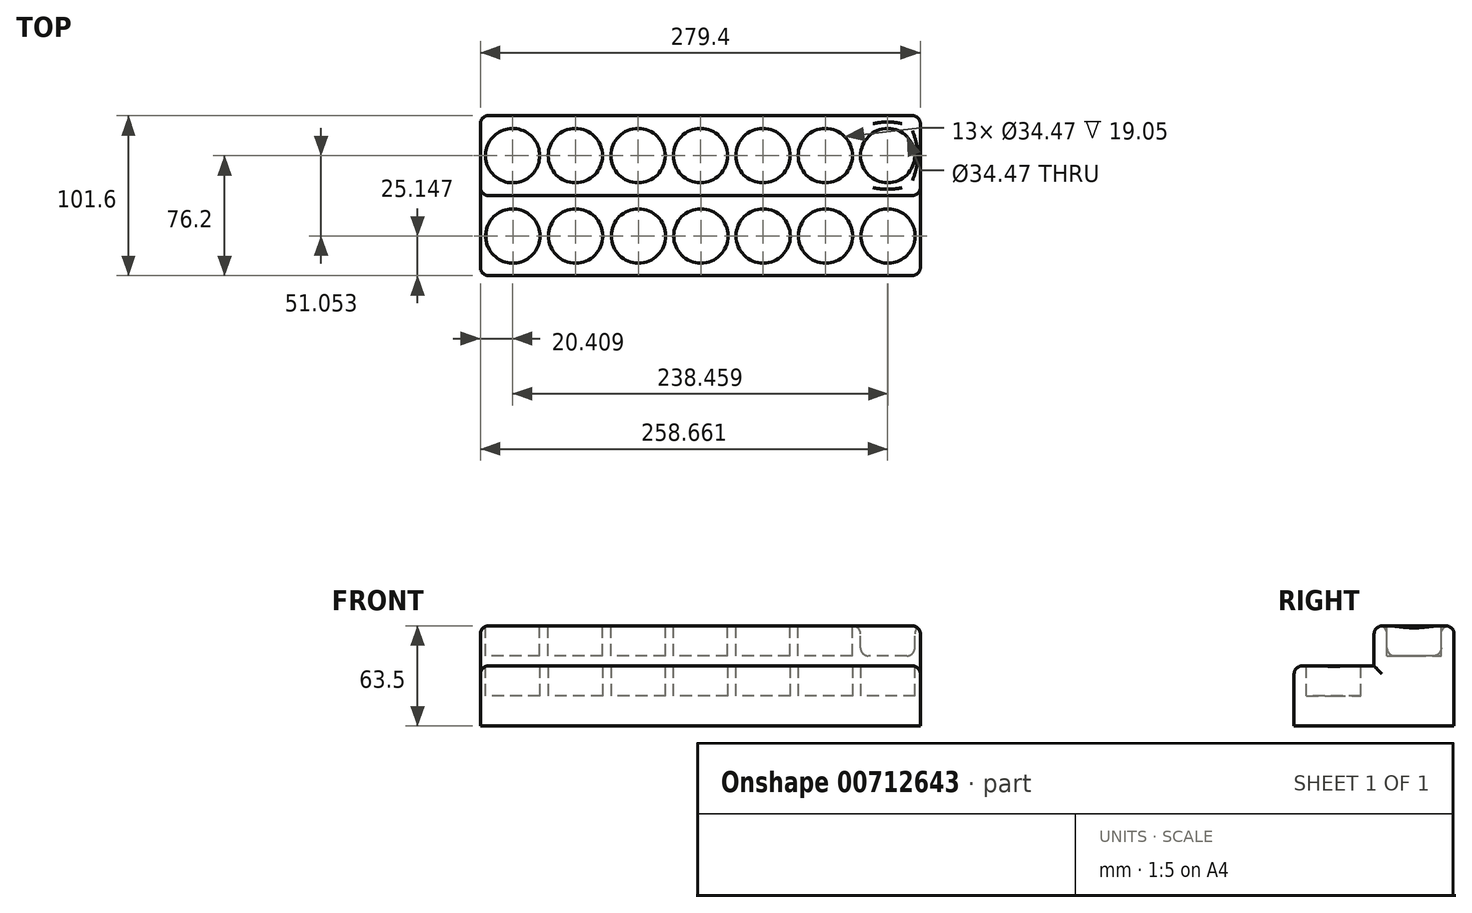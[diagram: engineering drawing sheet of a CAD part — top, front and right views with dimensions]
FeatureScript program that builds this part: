
annotation { "Feature Type Name" : "Feature", "Feature Type Description" : "" }
export const myFeature = defineFeature(function(context is Context, id is Id, definition is map)
    precondition{}
    {
        {
            var Q0;
            Q0=qCreatedBy(makeId("Top.planeOp"),FACE);
            var sketch = newSketch(context, id + "F0", { "sketchPlane" : qUnion([Q0])});
            skLineSegment(sketch, "E0.bottom", {"start": v(-139.7, 50.8) * mm, "end": v(139.7, 50.8) * mm});
            skLineSegment(sketch, "E0.top", {"start": v(-139.7, -50.8) * mm, "end": v(139.7, -50.8) * mm});
            skLineSegment(sketch, "E0.left", {"start": v(-139.7, 50.8) * mm, "end": v(-139.7, -50.8) * mm});
            skLineSegment(sketch, "E0.right", {"start": v(139.7, 50.8) * mm, "end": v(139.7, -50.8) * mm});
            skPoint(sketch, "E0.middle", {"position": v(0, 0) * mm});
            skLineSegment(sketch, "E1", {"start": v(-139.7, 0) * mm, "end": v(139.7, 0) * mm});
            skSolve(sketch);
        }
        {
            var Q0;
            {var subQ0=sQuery(id+"F0.wireOp",EDGE,"E0.bottom");Q0=makeQuery(id+"F0.imprint","IMPRINT",FACE,{"disambiguationData":[TD([[makeQuery(id+"F0.imprint","IMPRINT",EDGE,{"derivedFrom":subQ0}),-1.0]])]});}
            extrude(context, id + "F1", {"entities" : qUnion([Q0]), "depth" : 63.5 * mm, "offsetDistance" : 25.4 * mm});
        }
        {
            var Q0;
            Q0 = qSketchRegion(id + "F0", true);
            extrude(context, id + "F2", {"entities" : qUnion([Q0]), "operationType" : NewBodyOperationType.ADD, "depth" : 38.1 * mm, "offsetDistance" : 25.4 * mm});
        }
        {
            var Q0;
            Q0=makeQuery(id+"F1.opExtrude","CAP_FACE",FACE,{"disambiguationData":[OSD([sQuery(id+"F0.wireOp",EDGE,"E0.bottom"),sQuery(id+"F0.wireOp",EDGE,"E0.left"),sQuery(id+"F0.wireOp",EDGE,"E0.right"),sQuery(id+"F0.wireOp",EDGE,"E1")])],"isStart":false});
            var sketch = newSketch(context, id + "F3", { "sketchPlane" : qUnion([Q0])});
            skPoint(sketch, "E2", {"position": v(0, 50.8) * mm});
            skCircle(sketch, "E3", {"center": v(-119.3, 25.4) * mm, "radius": 17.23 * mm});
            skPoint(sketch, "E3.centerSnap0", {"position": v(-139.7, 25.4) * mm});
            skCircle(sketch, "E4.1.0.0", {"center": v(-79.41, 25.4) * mm, "radius": 17.23 * mm});
            skCircle(sketch, "E4.2.0.0", {"center": v(-39.54, 25.4) * mm, "radius": 17.23 * mm});
            skLineSegment(sketch, "E4.direction1", {"start": v(-119.3, 25.4) * mm, "end": v(-79.41, 25.4) * mm, "construction": true});
            skCircle(sketch, "E5.1.0.0", {"center": v(0.09, 25.4) * mm, "radius": 17.23 * mm});
            skCircle(sketch, "E5.2.0.0", {"center": v(39.71, 25.4) * mm, "radius": 17.23 * mm});
            skLineSegment(sketch, "E5.direction1", {"start": v(-39.54, 25.4) * mm, "end": v(0.09, 25.4) * mm, "construction": true});
            skCircle(sketch, "E6.1.0.0", {"center": v(79.34, 25.4) * mm, "radius": 17.23 * mm});
            skCircle(sketch, "E6.2.0.0", {"center": v(118.96, 25.4) * mm, "radius": 17.23 * mm});
            skLineSegment(sketch, "E6.direction1", {"start": v(39.71, 25.4) * mm, "end": v(79.34, 25.4) * mm, "construction": true});
            skPoint(sketch, "E7", {"position": v(0, 0) * mm});
            skSolve(sketch);
        }
        {
            var Q0;
            Q0=makeQuery(id+"F3.imprint","IMPRINT",FACE,{"disambiguationData":[TD([[makeQuery(id+"F3.imprint","IMPRINT",EDGE,{"derivedFrom":sQuery(id+"F3.wireOp",EDGE,"E3")}),1.0]])]});
            var Q1;
            Q1=makeQuery(id+"F3.imprint","IMPRINT",FACE,{"disambiguationData":[TD([[makeQuery(id+"F3.imprint","IMPRINT",EDGE,{"derivedFrom":sQuery(id+"F3.wireOp",EDGE,"E4.1.0.0")}),1.0]])]});
            var Q2;
            Q2=makeQuery(id+"F3.imprint","IMPRINT",FACE,{"disambiguationData":[TD([[makeQuery(id+"F3.imprint","IMPRINT",EDGE,{"derivedFrom":sQuery(id+"F3.wireOp",EDGE,"E4.2.0.0")}),1.0]])]});
            var Q3;
            Q3=makeQuery(id+"F3.imprint","IMPRINT",FACE,{"disambiguationData":[TD([[makeQuery(id+"F3.imprint","IMPRINT",EDGE,{"derivedFrom":sQuery(id+"F3.wireOp",EDGE,"E5.1.0.0")}),1.0]])]});
            var Q4;
            Q4=makeQuery(id+"F3.imprint","IMPRINT",FACE,{"disambiguationData":[TD([[makeQuery(id+"F3.imprint","IMPRINT",EDGE,{"derivedFrom":sQuery(id+"F3.wireOp",EDGE,"E5.2.0.0")}),1.0]])]});
            var Q5;
            Q5=makeQuery(id+"F3.imprint","IMPRINT",FACE,{"disambiguationData":[TD([[makeQuery(id+"F3.imprint","IMPRINT",EDGE,{"derivedFrom":sQuery(id+"F3.wireOp",EDGE,"E6.1.0.0")}),1.0]])]});
            var Q6;
            Q6=makeQuery(id+"F3.imprint","IMPRINT",FACE,{"disambiguationData":[TD([[makeQuery(id+"F3.imprint","IMPRINT",EDGE,{"derivedFrom":sQuery(id+"F3.wireOp",EDGE,"E6.2.0.0")}),1.0]])]});
            extrude(context, id + "F4", {"entities" : qUnion([Q0, Q1, Q2, Q3, Q4, Q5, Q6]), "operationType" : NewBodyOperationType.REMOVE, "oppositeDirection" : true, "depth" : 19.05 * mm, "offsetDistance" : 25.4 * mm});
        }
        {
            var Q0;
            Q0=makeQuery(id+"F2.opExtrude","CAP_FACE",FACE,{"disambiguationData":[OSD([sQuery(id+"F0.wireOp",EDGE,"E0.bottom"),sQuery(id+"F0.wireOp",EDGE,"E0.top"),sQuery(id+"F0.wireOp",EDGE,"E0.left"),sQuery(id+"F0.wireOp",EDGE,"E0.right")])],"isStart":false});
            var sketch = newSketch(context, id + "F5", { "sketchPlane" : qUnion([Q0])});
            skCircle(sketch, "E8", {"center": v(-119.08, -25.65) * mm, "radius": 17.23 * mm});
            skCircle(sketch, "E9.1.0.0", {"center": v(-79.2, -25.63) * mm, "radius": 17.23 * mm});
            skCircle(sketch, "E9.2.0.0", {"center": v(-39.33, -25.63) * mm, "radius": 17.23 * mm});
            skCircle(sketch, "E10.1.0.0", {"center": v(0.3, -25.63) * mm, "radius": 17.23 * mm});
            skCircle(sketch, "E10.2.0.0", {"center": v(39.92, -25.63) * mm, "radius": 17.23 * mm});
            skCircle(sketch, "E11.1.0.0", {"center": v(79.54, -25.63) * mm, "radius": 17.23 * mm});
            skCircle(sketch, "E11.2.0.0", {"center": v(119.17, -25.63) * mm, "radius": 17.23 * mm});
            skSolve(sketch);
        }
        {
            var Q0;
            Q0=makeQuery(id+"F5.imprint","IMPRINT",FACE,{"disambiguationData":[TD([[makeQuery(id+"F5.imprint","IMPRINT",EDGE,{"derivedFrom":sQuery(id+"F5.wireOp",EDGE,"E8")}),1.0]])]});
            var Q1;
            Q1=makeQuery(id+"F5.imprint","IMPRINT",FACE,{"disambiguationData":[TD([[makeQuery(id+"F5.imprint","IMPRINT",EDGE,{"derivedFrom":sQuery(id+"F5.wireOp",EDGE,"E9.1.0.0")}),1.0]])]});
            var Q2;
            Q2=makeQuery(id+"F5.imprint","IMPRINT",FACE,{"disambiguationData":[TD([[makeQuery(id+"F5.imprint","IMPRINT",EDGE,{"derivedFrom":sQuery(id+"F5.wireOp",EDGE,"E9.2.0.0")}),1.0]])]});
            var Q3;
            Q3=makeQuery(id+"F5.imprint","IMPRINT",FACE,{"disambiguationData":[TD([[makeQuery(id+"F5.imprint","IMPRINT",EDGE,{"derivedFrom":sQuery(id+"F5.wireOp",EDGE,"E10.1.0.0")}),1.0]])]});
            var Q4;
            Q4=makeQuery(id+"F5.imprint","IMPRINT",FACE,{"disambiguationData":[TD([[makeQuery(id+"F5.imprint","IMPRINT",EDGE,{"derivedFrom":sQuery(id+"F5.wireOp",EDGE,"E10.2.0.0")}),1.0]])]});
            var Q5;
            Q5=makeQuery(id+"F5.imprint","IMPRINT",FACE,{"disambiguationData":[TD([[makeQuery(id+"F5.imprint","IMPRINT",EDGE,{"derivedFrom":sQuery(id+"F5.wireOp",EDGE,"E11.1.0.0")}),1.0]])]});
            var Q6;
            Q6=makeQuery(id+"F5.imprint","IMPRINT",FACE,{"disambiguationData":[TD([[makeQuery(id+"F5.imprint","IMPRINT",EDGE,{"derivedFrom":sQuery(id+"F5.wireOp",EDGE,"E11.2.0.0")}),1.0]])]});
            var Q7;
            Q7=sQuery(id+"F5.wireOp",EDGE,"E8");
            var Q8;
            Q8=sQuery(id+"F5.wireOp",EDGE,"E9.1.0.0");
            var Q9;
            Q9=sQuery(id+"F5.wireOp",EDGE,"E9.2.0.0");
            var Q10;
            Q10=sQuery(id+"F5.wireOp",EDGE,"E10.1.0.0");
            var Q11;
            Q11=sQuery(id+"F5.wireOp",EDGE,"E10.2.0.0");
            var Q12;
            Q12=sQuery(id+"F5.wireOp",EDGE,"E11.1.0.0");
            var Q13;
            Q13=sQuery(id+"F5.wireOp",EDGE,"E11.2.0.0");
            extrude(context, id + "F6", {"entities" : qUnion([Q0, Q1, Q2, Q3, Q4, Q5, Q6]), "operationType" : NewBodyOperationType.REMOVE, "surfaceEntities" : qUnion([Q7, Q8, Q9, Q10, Q11, Q12, Q13]), "oppositeDirection" : true, "depth" : 19.05 * mm, "offsetDistance" : 25.4 * mm});
        }
        {
            var Q0;
            Q0=makeQuery(id+"F1.opExtrude","CAP_EDGE",EDGE,{"disambiguationData":[OSD([sQuery(id+"F0.wireOp",EDGE,"E0.left")])],"isStart":false});
            var Q1;
            Q1=makeQuery(id+"F1.opExtrude","CAP_EDGE",EDGE,{"disambiguationData":[OSD([sQuery(id+"F0.wireOp",EDGE,"E1")])],"isStart":false});
            var Q2;
            Q2=makeQuery(id+"F1.opExtrude","CAP_EDGE",EDGE,{"disambiguationData":[OSD([sQuery(id+"F0.wireOp",EDGE,"E0.right")])],"isStart":false});
            var Q3;
            Q3=makeQuery(id+"F1.opExtrude","CAP_EDGE",EDGE,{"disambiguationData":[OSD([sQuery(id+"F0.wireOp",EDGE,"E0.bottom")])],"isStart":false});
            var Q4;
            Q4=makeQuery(id+"F2.opExtrude","CAP_EDGE",EDGE,{"disambiguationData":[OSD([sQuery(id+"F0.wireOp",EDGE,"E0.left")])],"isStart":false});
            var Q5;
            Q5=makeQuery(id+"F2.opExtrude","CAP_EDGE",EDGE,{"disambiguationData":[OSD([sQuery(id+"F0.wireOp",EDGE,"E0.top")])],"isStart":false});
            var Q6;
            Q6=makeQuery(id+"F2.opExtrude","CAP_EDGE",EDGE,{"disambiguationData":[OSD([sQuery(id+"F0.wireOp",EDGE,"E0.right")])],"isStart":false});
            var Q7;
            Q7=makeQuery(id+"F6.boolean.opBoolean","COPY",EDGE,{"derivedFrom":makeQuery(id+"F6.opExtrude","CAP_EDGE",EDGE,{"disambiguationData":[OSD([sQuery(id+"F5.wireOp",EDGE,"E11.2.0.0")])],"isStart":true})});
            var Q8;
            Q8=makeQuery(id+"F6.boolean.opBoolean","COPY",EDGE,{"derivedFrom":makeQuery(id+"F6.opExtrude","CAP_EDGE",EDGE,{"disambiguationData":[OSD([sQuery(id+"F5.wireOp",EDGE,"E11.1.0.0")])],"isStart":true})});
            var Q9;
            Q9=makeQuery(id+"F6.boolean.opBoolean","COPY",EDGE,{"derivedFrom":makeQuery(id+"F6.opExtrude","CAP_EDGE",EDGE,{"disambiguationData":[OSD([sQuery(id+"F5.wireOp",EDGE,"E10.2.0.0")])],"isStart":true})});
            var Q10;
            Q10=makeQuery(id+"F6.boolean.opBoolean","COPY",EDGE,{"derivedFrom":makeQuery(id+"F6.opExtrude","CAP_EDGE",EDGE,{"disambiguationData":[OSD([sQuery(id+"F5.wireOp",EDGE,"E10.1.0.0")])],"isStart":true})});
            var Q11;
            Q11=makeQuery(id+"F6.boolean.opBoolean","COPY",EDGE,{"derivedFrom":makeQuery(id+"F6.opExtrude","CAP_EDGE",EDGE,{"disambiguationData":[OSD([sQuery(id+"F5.wireOp",EDGE,"E9.2.0.0")])],"isStart":true})});
            var Q12;
            Q12=makeQuery(id+"F6.boolean.opBoolean","COPY",EDGE,{"derivedFrom":makeQuery(id+"F6.opExtrude","CAP_EDGE",EDGE,{"disambiguationData":[OSD([sQuery(id+"F5.wireOp",EDGE,"E9.1.0.0")])],"isStart":true})});
            var Q13;
            Q13=makeQuery(id+"F6.boolean.opBoolean","COPY",EDGE,{"derivedFrom":makeQuery(id+"F6.opExtrude","CAP_EDGE",EDGE,{"disambiguationData":[OSD([sQuery(id+"F5.wireOp",EDGE,"E8")])],"isStart":true})});
            var Q14;
            Q14=makeQuery(id+"F4.boolean.opBoolean","COPY",EDGE,{"derivedFrom":makeQuery(id+"F4.opExtrude","CAP_EDGE",EDGE,{"disambiguationData":[OSD([sQuery(id+"F3.wireOp",EDGE,"E3")])],"isStart":true})});
            var Q15;
            Q15=makeQuery(id+"F4.boolean.opBoolean","COPY",EDGE,{"derivedFrom":makeQuery(id+"F4.opExtrude","CAP_EDGE",EDGE,{"disambiguationData":[OSD([sQuery(id+"F3.wireOp",EDGE,"E4.1.0.0")])],"isStart":true})});
            var Q16;
            Q16=makeQuery(id+"F4.boolean.opBoolean","COPY",EDGE,{"derivedFrom":makeQuery(id+"F4.opExtrude","CAP_EDGE",EDGE,{"disambiguationData":[OSD([sQuery(id+"F3.wireOp",EDGE,"E4.2.0.0")])],"isStart":true})});
            var Q17;
            Q17=makeQuery(id+"F4.boolean.opBoolean","COPY",EDGE,{"derivedFrom":makeQuery(id+"F4.opExtrude","CAP_EDGE",EDGE,{"disambiguationData":[OSD([sQuery(id+"F3.wireOp",EDGE,"E5.1.0.0")])],"isStart":true})});
            var Q18;
            Q18=makeQuery(id+"F4.boolean.opBoolean","COPY",EDGE,{"derivedFrom":makeQuery(id+"F4.opExtrude","CAP_EDGE",EDGE,{"disambiguationData":[OSD([sQuery(id+"F3.wireOp",EDGE,"E5.2.0.0")])],"isStart":true})});
            var Q19;
            Q19=makeQuery(id+"F4.boolean.opBoolean","COPY",EDGE,{"derivedFrom":makeQuery(id+"F4.opExtrude","CAP_EDGE",EDGE,{"disambiguationData":[OSD([sQuery(id+"F3.wireOp",EDGE,"E6.1.0.0")])],"isStart":true})});
            var Q20;
            Q20=makeQuery(id+"F4.boolean.opBoolean","COPY",FACE,{"derivedFrom":makeQuery(id+"F4.opExtrude","SWEPT_FACE",FACE,{"disambiguationData":[OSD([sQuery(id+"F3.wireOp",EDGE,"E6.2.0.0")])]})});
            var Q21;
            Q21=makeQuery(id+"F2.opExtrude","SWEPT_EDGE",EDGE,{"disambiguationData":[OSD([sQuery(id+"F0.wireOp",EDGE,"E0.top"),sQuery(id+"F0.wireOp",EDGE,"E0.left")])]});
            var Q22;
            Q22=makeQuery(id+"F2.opExtrude","SWEPT_EDGE",EDGE,{"disambiguationData":[OSD([sQuery(id+"F0.wireOp",EDGE,"E0.top"),sQuery(id+"F0.wireOp",EDGE,"E0.right")])]});
            var Q23;
            Q23=makeQuery(id+"F1.opExtrude","SWEPT_EDGE",EDGE,{"disambiguationData":[OSD([sQuery(id+"F0.wireOp",EDGE,"E0.right"),sQuery(id+"F0.wireOp",EDGE,"E1")])]});
            var Q24;
            Q24=makeQuery(id+"F1.opExtrude","SWEPT_EDGE",EDGE,{"disambiguationData":[OSD([sQuery(id+"F0.wireOp",EDGE,"E0.left"),sQuery(id+"F0.wireOp",EDGE,"E1")])]});
            var Q25;
            Q25=makeQuery(id+"F1.opExtrude","SWEPT_EDGE",EDGE,{"disambiguationData":[OSD([sQuery(id+"F0.wireOp",EDGE,"E0.bottom"),sQuery(id+"F0.wireOp",EDGE,"E0.left")])]});
            var Q26;
            Q26=makeQuery(id+"F1.opExtrude","SWEPT_EDGE",EDGE,{"disambiguationData":[OSD([sQuery(id+"F0.wireOp",EDGE,"E0.bottom"),sQuery(id+"F0.wireOp",EDGE,"E0.right")])]});
            fillet(context, id + "F7", {"entities" : qUnion([Q0, Q1, Q2, Q3, Q4, Q5, Q6, Q7, Q8, Q9, Q10, Q11, Q12, Q13, Q14, Q15, Q16, Q17, Q18, Q19, Q20, Q21, Q22, Q23, Q24, Q25, Q26]), "radius" : 5.08 * mm, "tangentPropagation" : true, "allowEdgeOverflow" : false});
        }
    });
